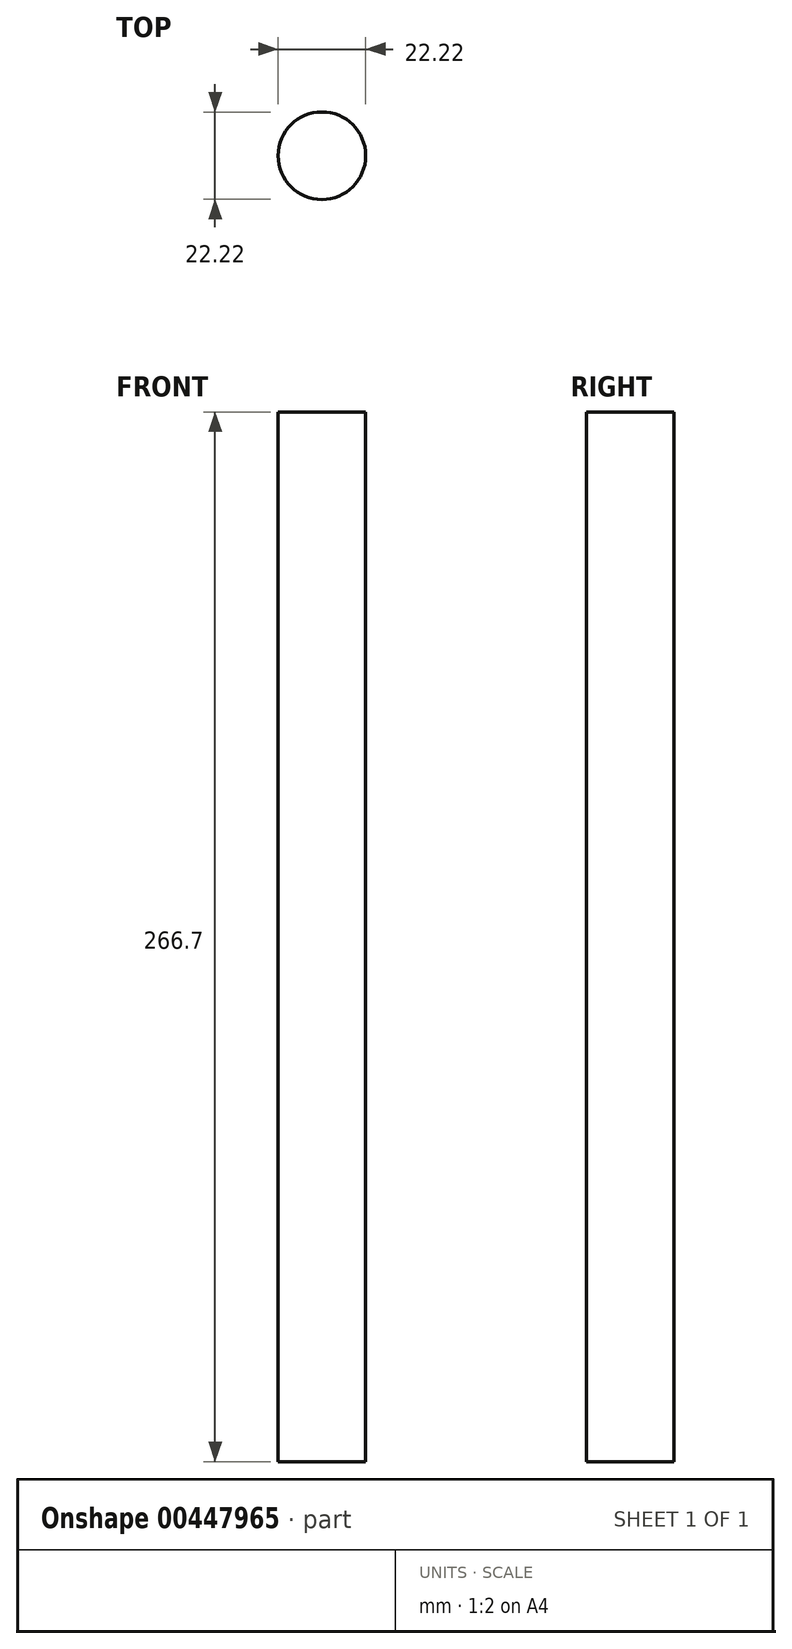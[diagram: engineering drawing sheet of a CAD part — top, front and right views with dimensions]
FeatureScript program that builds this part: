
annotation { "Feature Type Name" : "Feature", "Feature Type Description" : "" }
export const myFeature = defineFeature(function(context is Context, id is Id, definition is map)
    precondition{}
    {
        {
            var Q0;
            Q0=qCreatedBy(makeId("Top.planeOp"),FACE);
            var sketch = newSketch(context, id + "F0", { "sketchPlane" : qUnion([Q0])});
            skCircle(sketch, "E0", {"center": v(0, 0) * mm, "radius": 11.11 * mm});
            skSolve(sketch);
        }
        {
            var Q0;
            Q0=makeQuery(id+"F0.imprint","IMPRINT",FACE,{"disambiguationData":[TD([[makeQuery(id+"F0.imprint","IMPRINT",EDGE,{"derivedFrom":sQuery(id+"F0.wireOp",EDGE,"E0")}),1.0]])]});
            extrude(context, id + "F1", {"entities" : qUnion([Q0]), "depth" : 266.7 * mm});
        }
    });
